# Revit family: ADHERIBLE 5050 IP33_LK5033WW_NW
name_source: partatom
category: Luminarias
units: mm (PartAtom-declared; Revit-internal decimal feet)

## family parameters
Compartido = No
Corte con vacíos al cargar = No
Cota de conector redondo = Diámetro de uso
Origen de luz = Sí
Punto de cálculo de habitación = No
Se basa en plano de trabajo = Sí
Siempre vertical = No
Tipo de pieza = Normal

## types (2) — shared parameters
Ancho = 10 mm  [stored 0.0328084 ft]
Cambio de temperatura de color de luz atenuada = <Ninguno>
Fabricante = BRILLANT
Filtro de color = 16777215
Longitud de línea de emisión = 600 mm  [stored 1.9685 ft]
Longitud de símbolo de origen de luz = 1500 mm  [stored 4.92126 ft]
Lámpara = 5050 SMD
Ángulo de campo de foco = 90.00°
Ángulo de enfoque = 30.00°
Ángulo de inclinación = 60.00°
zero-valued in all types: Costo, Elevación por defecto

## per-type parameters (varying)
| type | Comentarios de vataje | Descripción | Modelo |
| ADHERIBLE 5050 IP33_LK5033WW | 24V | TIRA LED ADHERIBLE 10MM DE ANCHO IP33 USO PARA INTERIORES, DE PCB BLANCO SIN RECUBRIMIENTO, MONO CROMATICA, CON UNA POTENCIA DE 8W/M DE UN TIPO DE LED 5050 SMD, IRC80, 60 LEDS POR METRO, PRESENTACION DE 5M, TEMPERATURA EN BLANCO CALIDO 3000K, 700 LUMENES POR METRO, EFICIENCIA DE 87.5 LM/W, CORTE A 5CM, ALIMENTADA A 12V, REQUIERE ACCESORIOS COMO FUENTE DE PODER Y CABLE DE ALIMENTACION. PERFIL EN CASO DE SER NECESARIO. | LK5033WW |
| ADHERIBLE 5050 IP33_LK5033NW | 12V | TIRA LED ADHERIBLE 10MM DE ANCHO IP33 USO PARA INTERIORES, DE PCB BLANCO SIN RECUBRIMIENTO, MONO CROMATICA, CON UNA POTENCIA DE 8W/M DE UN TIPO DE LED 5050 SMD, IRC80, 60 LEDS POR METRO, PRESENTACION DE 5M, TEMPERATURA EN BLANCO FRIO 4500K, 700 LUMENES POR METRO, EFICIENCIA DE 87.5 LM/W, CORTE A 5CM, ALIMENTADA A 12V, REQUIERE ACCESORIOS COMO FUENTE DE PODER Y CABLE DE ALIMENTACION. PERFIL EN CASO DE SER NECESARIO. | LK5033NW |

note: [stored X ft] marks values corroborated as IEEE doubles in the binary element streams (Revit-internal decimal feet)

## geometry (parser evidence)
native form markers: Blend x2
no freeform markers — native parametric forms only
